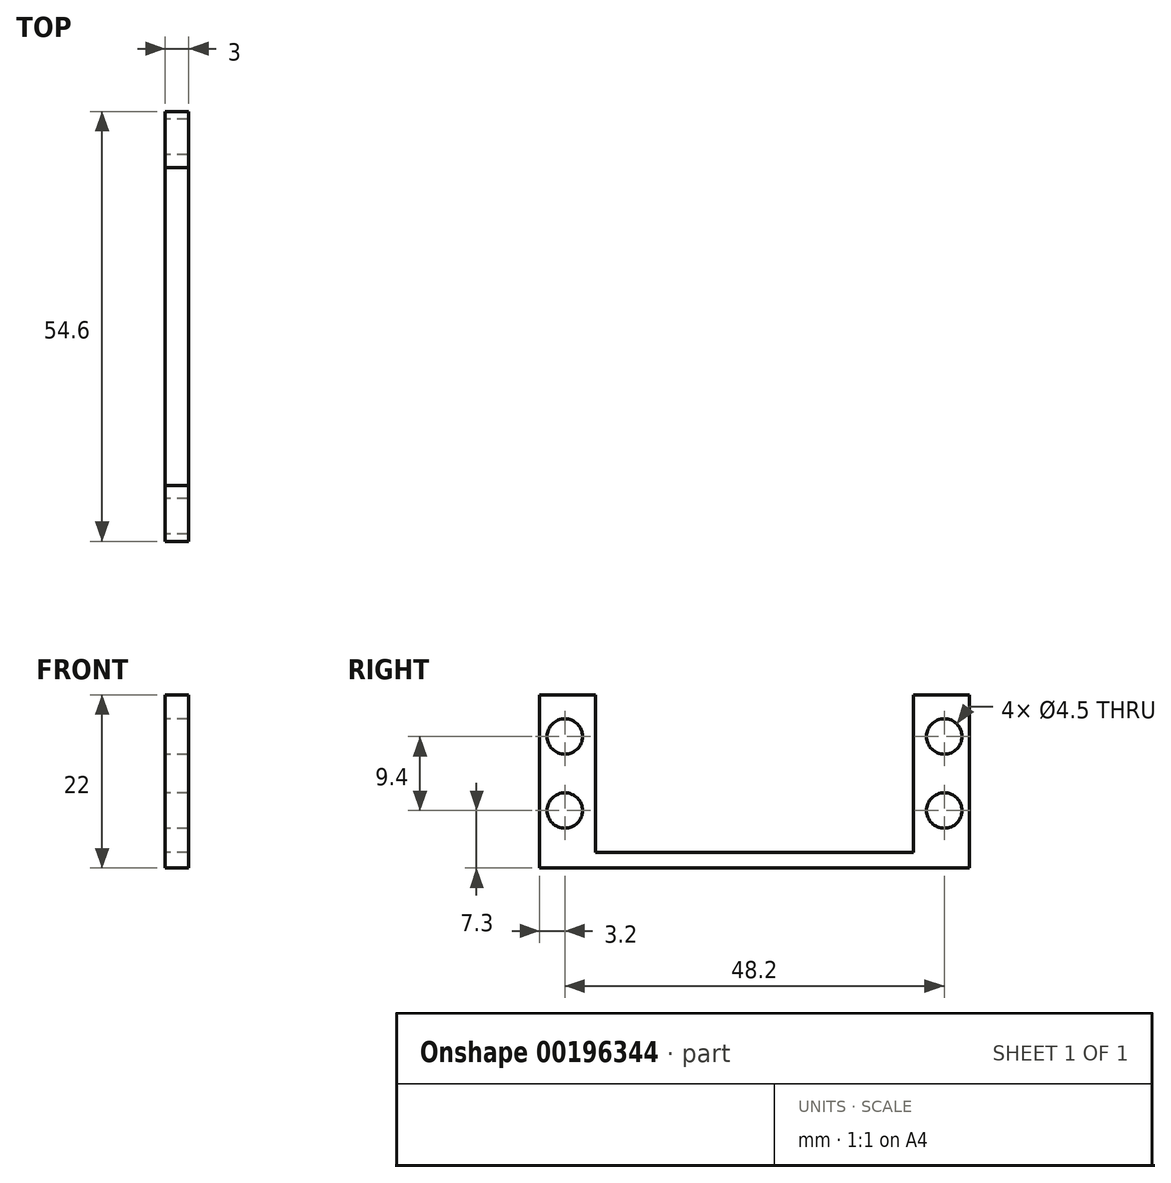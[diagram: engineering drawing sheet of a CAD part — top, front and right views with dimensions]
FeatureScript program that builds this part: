
annotation { "Feature Type Name" : "Feature", "Feature Type Description" : "" }
export const myFeature = defineFeature(function(context is Context, id is Id, definition is map)
    precondition{}
    {
        {
            var Q0;
            Q0=qCreatedBy(makeId("Right.planeOp"),FACE);
            var sketch = newSketch(context, id + "F0", { "sketchPlane" : qUnion([Q0])});
            skLineSegment(sketch, "E0", {"start": v(27.3, 1.3) * mm, "end": v(27.3, 1.3) * mm});
            skLineSegment(sketch, "E1", {"start": v(-27.3, 1.3) * mm, "end": v(27.3, 1.3) * mm});
            skLineSegment(sketch, "E2", {"start": v(27.3, 1.3) * mm, "end": v(20.2, 1.3) * mm});
            skLineSegment(sketch, "E3", {"start": v(20.2, 1.3) * mm, "end": v(20.2, 21.3) * mm});
            skLineSegment(sketch, "E4", {"start": v(20.2, 21.3) * mm, "end": v(27.3, 21.3) * mm});
            skLineSegment(sketch, "E5", {"start": v(27.3, 21.3) * mm, "end": v(27.3, 1.3) * mm});
            skLineSegment(sketch, "E6", {"start": v(-27.3, 1.3) * mm, "end": v(-27.3, 21.3) * mm});
            skLineSegment(sketch, "E7", {"start": v(-27.3, 21.3) * mm, "end": v(-20.2, 21.3) * mm});
            skLineSegment(sketch, "E8", {"start": v(-20.2, 21.3) * mm, "end": v(-20.2, 1.3) * mm});
            skLineSegment(sketch, "E9", {"start": v(-20.2, 1.3) * mm, "end": v(-27.3, 1.3) * mm});
            skLineSegment(sketch, "E10", {"start": v(-20.2, 1.3) * mm, "end": v(-24.1, 1.3) * mm, "construction": true});
            skLineSegment(sketch, "E11", {"start": v(-24.1, 1.3) * mm, "end": v(-24.1, 21.3) * mm, "construction": true});
            skLineSegment(sketch, "E12", {"start": v(20.2, 1.3) * mm, "end": v(24.1, 1.3) * mm, "construction": true});
            skLineSegment(sketch, "E13", {"start": v(24.1, 1.3) * mm, "end": v(24.1, 21.3) * mm, "construction": true});
            skLineSegment(sketch, "E14", {"start": v(-24.1, 1.3) * mm, "end": v(-24.1, 6.6) * mm, "construction": true});
            skLineSegment(sketch, "E15", {"start": v(-24.1, 6.6) * mm, "end": v(-24.1, 16) * mm, "construction": true});
            skLineSegment(sketch, "E16", {"start": v(24.1, 1.3) * mm, "end": v(24.1, 6.6) * mm, "construction": true});
            skLineSegment(sketch, "E17", {"start": v(24.1, 6.6) * mm, "end": v(24.1, 16) * mm, "construction": true});
            skCircle(sketch, "E18", {"center": v(-24.1, 16) * mm, "radius": 2.25 * mm});
            skCircle(sketch, "E19", {"center": v(-24.1, 6.6) * mm, "radius": 2.25 * mm});
            skCircle(sketch, "E20", {"center": v(24.1, 6.6) * mm, "radius": 2.25 * mm});
            skCircle(sketch, "E21", {"center": v(24.1, 16) * mm, "radius": 2.25 * mm});
            skLineSegment(sketch, "E22", {"start": v(-27.3, 1.3) * mm, "end": v(-27.3, -0.7) * mm});
            skLineSegment(sketch, "E23", {"start": v(-27.3, -0.7) * mm, "end": v(27.3, -0.7) * mm});
            skLineSegment(sketch, "E24", {"start": v(27.3, -0.7) * mm, "end": v(27.3, 1.3) * mm});
            skSolve(sketch);
        }
        {
            var Q0;
            Q0=qSketchRegion(id+"F0",true);
            extrude(context, id + "F1", {"entities" : qUnion([Q0]), "depth" : 3 * mm});
        }
    });
